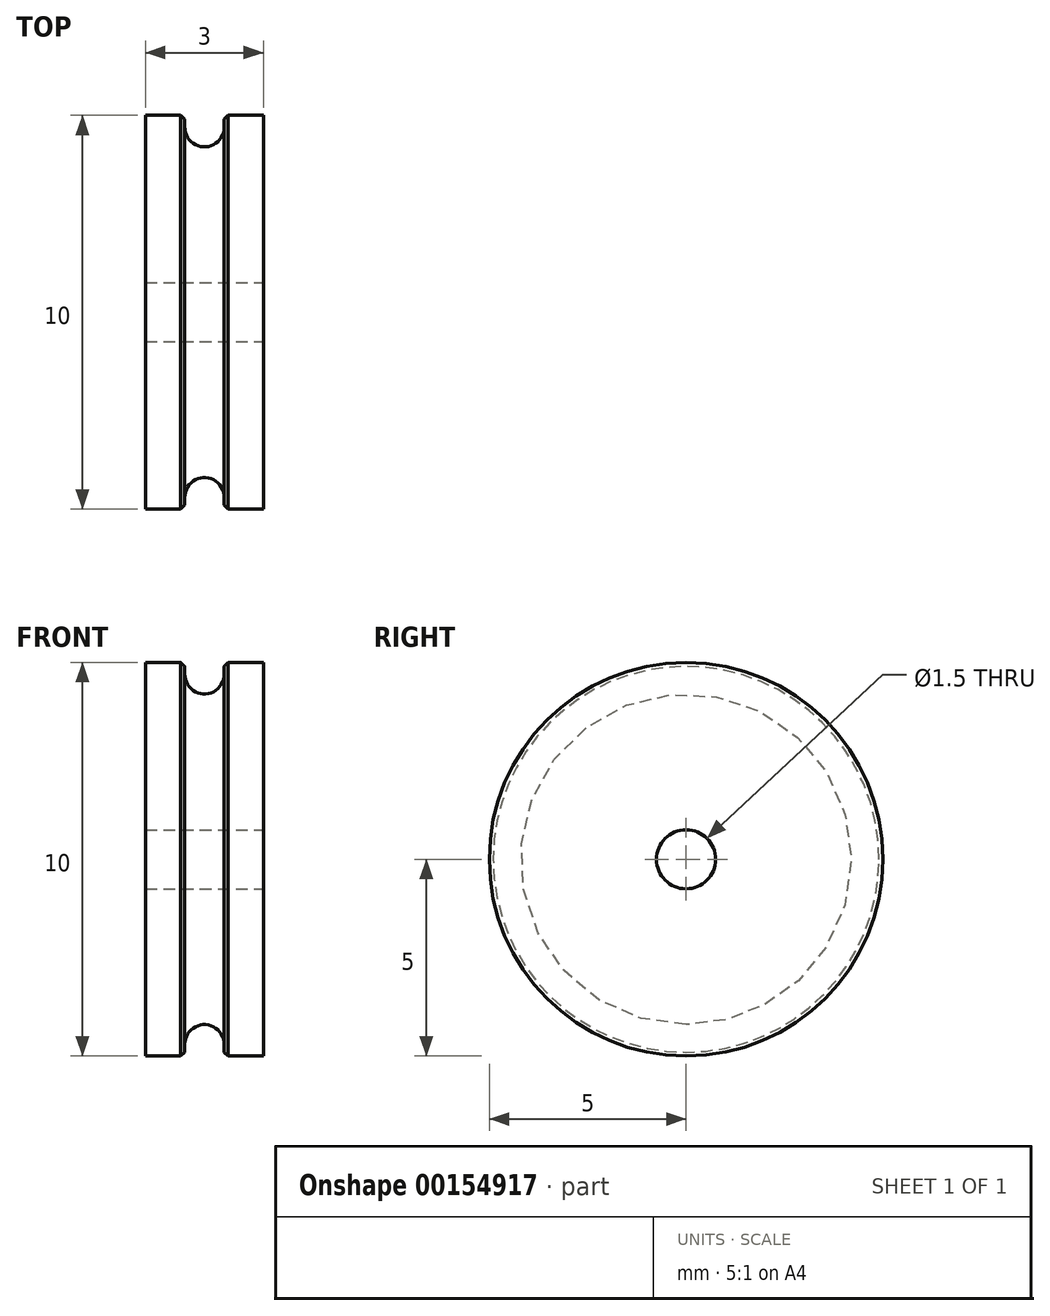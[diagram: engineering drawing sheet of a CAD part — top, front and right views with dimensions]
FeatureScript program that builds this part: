
annotation { "Feature Type Name" : "Feature", "Feature Type Description" : "" }
export const myFeature = defineFeature(function(context is Context, id is Id, definition is map)
    precondition{}
    {
        {
            var Q0;
            Q0=qCreatedBy(makeId("Front.planeOp"),FACE);
            var sketch = newSketch(context, id + "F0", { "sketchPlane" : qUnion([Q0])});
            skLineSegment(sketch, "E0", {"start": v(0, 0) * mm, "end": v(-1.5, 0) * mm});
            skLineSegment(sketch, "E1", {"start": v(-1.5, 0) * mm, "end": v(-1.5, 5) * mm});
            skLineSegment(sketch, "E2", {"start": v(-1.5, 5) * mm, "end": v(-0.5, 5) * mm});
            skPoint(sketch, "E3.centerSnap0", {"position": v(-1, 5) * mm});
            skPoint(sketch, "E4.MirrorP", {"position": v(1, 5) * mm});
            skLineSegment(sketch, "E5.MirrorCS", {"start": v(1.5, 0) * mm, "end": v(1.5, 5) * mm});
            skLineSegment(sketch, "E6.MirrorCS", {"start": v(1.5, 5) * mm, "end": v(0.5, 5) * mm});
            skLineSegment(sketch, "E7.MirrorCS", {"start": v(0, 0) * mm, "end": v(1.5, 0) * mm});
            skLineSegment(sketch, "E8", {"start": v(-0.5, 5) * mm, "end": v(-0.5, 4.7) * mm});
            skLineSegment(sketch, "E9", {"start": v(0.5, 5) * mm, "end": v(0.5, 4.7) * mm});
            skArc(sketch, "E10", {"start": v(-0.5, 4.7) * mm, "mid": v(0, 4.2) * mm, "end": v(0.5, 4.7) * mm});
            skSolve(sketch);
        }
        {
            var Q0;
            Q0=makeQuery(id+"F0.imprint","IMPRINT",FACE,{"disambiguationData":[TD([[makeQuery(id+"F0.imprint","IMPRINT",EDGE,{"derivedFrom":sQuery(id+"F0.wireOp",EDGE,"E0")}),-1.0]])]});
            var Q1;
            Q1=sQuery(id+"F0.wireOp",EDGE,"E0");
            revolve(context, id + "F1", {"entities" : qUnion([Q0]), "axis" : qUnion([Q1]), "revolveType" : RevolveType.FULL});
        }
        {
            var Q0;
            Q0=makeQuery(id+"F1.opRevolve","SWEPT_FACE",FACE,{"disambiguationData":[OSD([sQuery(id+"F0.wireOp",EDGE,"E5.MirrorCS")])]});
            var sketch = newSketch(context, id + "F2", { "sketchPlane" : qUnion([Q0])});
            skCircle(sketch, "E11", {"center": v(0, 0) * mm, "radius": 0.75 * mm});
            skSolve(sketch);
        }
        {
            var Q0;
            Q0=makeQuery(id+"F2.imprint","IMPRINT",FACE,{"disambiguationData":[TD([[makeQuery(id+"F2.imprint","IMPRINT",EDGE,{"derivedFrom":sQuery(id+"F2.wireOp",EDGE,"E11")}),1.0]])]});
            var Q1;
            Q1=makeQuery(id+"F1.opRevolve","SWEPT_FACE",FACE,{"disambiguationData":[OSD([sQuery(id+"F0.wireOp",EDGE,"E1")])]});
            extrude(context, id + "F3", {"entities" : qUnion([Q0]), "operationType" : NewBodyOperationType.REMOVE, "endBound" : BoundingType.UP_TO_SURFACE, "oppositeDirection" : true, "endBoundEntityFace" : qUnion([Q1]), "depth" : 25 * mm});
        }
        {
            var Q0;
            Q0=makeQuery(id+"F1.opRevolve","SWEPT_EDGE",EDGE,{"disambiguationData":[OSD([sQuery(id+"F0.wireOp",EDGE,"E6.MirrorCS"),sQuery(id+"F0.wireOp",EDGE,"E9")])]});
            var Q1;
            Q1=makeQuery(id+"F1.opRevolve","SWEPT_EDGE",EDGE,{"disambiguationData":[OSD([sQuery(id+"F0.wireOp",EDGE,"E2"),sQuery(id+"F0.wireOp",EDGE,"E8")])]});
            chamfer(context, id + "F4", {"entities" : qUnion([Q0, Q1]), "width" : 0.1 * mm, "tangentPropagation" : true});
        }
    });
